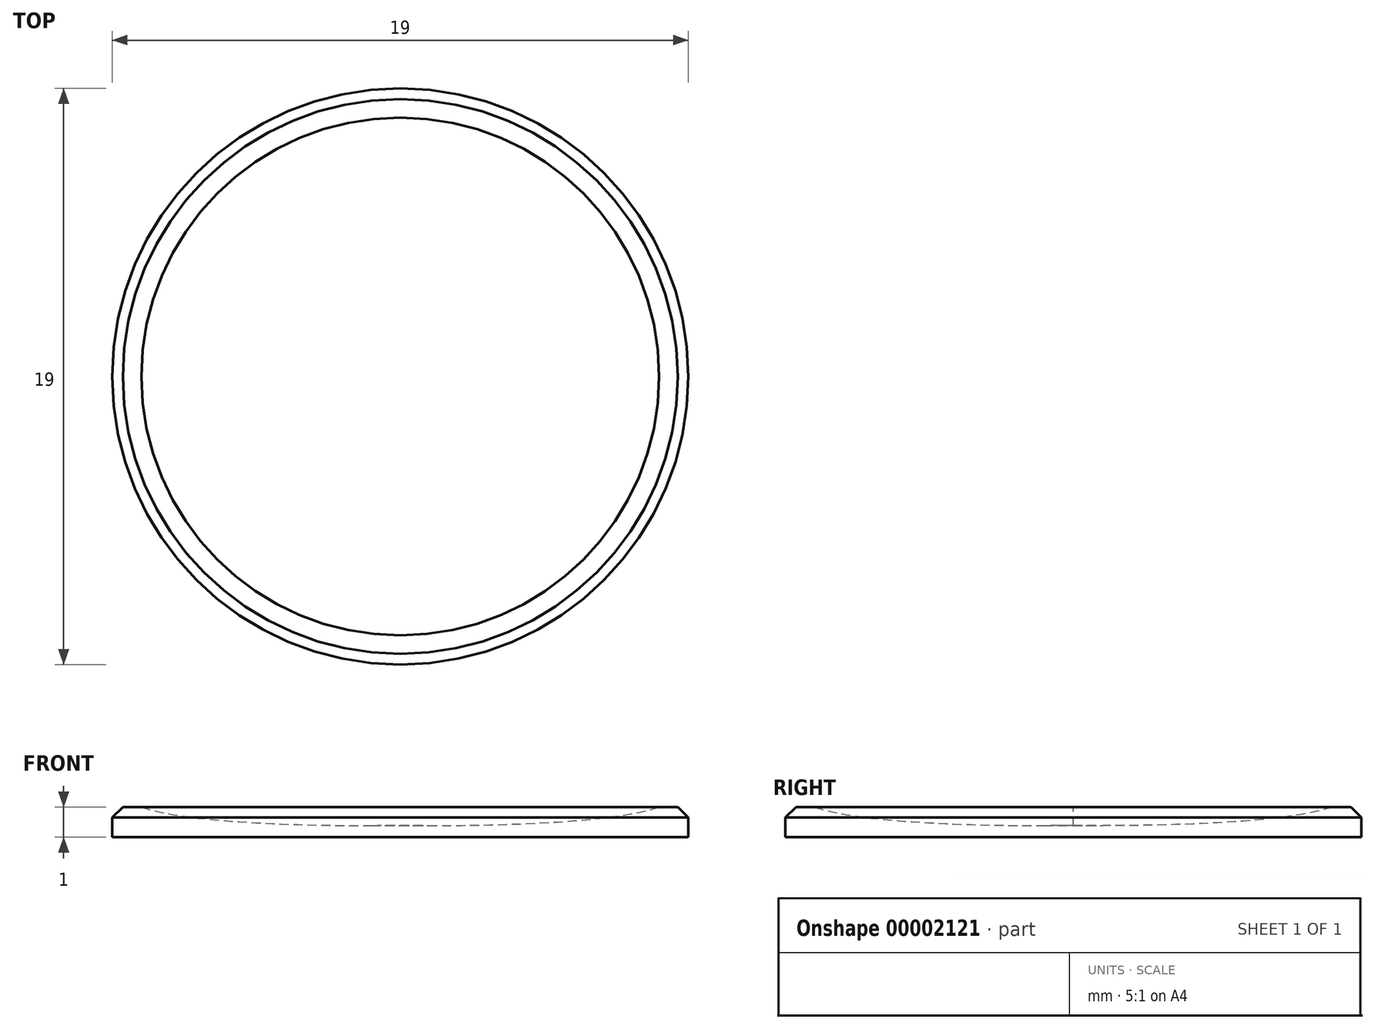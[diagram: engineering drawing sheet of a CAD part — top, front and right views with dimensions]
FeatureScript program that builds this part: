
annotation { "Feature Type Name" : "Feature", "Feature Type Description" : "" }
export const myFeature = defineFeature(function(context is Context, id is Id, definition is map)
    precondition{}
    {
        {
            var Q0;
            Q0=qCreatedBy(makeId("Top.planeOp"),FACE);
            var sketch = newSketch(context, id + "F0", { "sketchPlane" : qUnion([Q0])});
            skCircle(sketch, "E0", {"center": v(0, 0) * mm, "radius": 9.5 * mm});
            skSolve(sketch);
        }
        {
            var Q0;
            Q0=makeQuery(id+"F0.imprint","IMPRINT",FACE,{"disambiguationData":[TD([[makeQuery(id+"F0.imprint","IMPRINT",EDGE,{"derivedFrom":sQuery(id+"F0.wireOp",EDGE,"E0")}),1.0]])]});
            extrude(context, id + "F1", {"entities" : qUnion([Q0]), "depth" : 1 * mm});
        }
        {
            var Q0;
            Q0=qCreatedBy(makeId("Front.planeOp"),FACE);
            var sketch = newSketch(context, id + "F2", { "sketchPlane" : qUnion([Q0])});
            skLineSegment(sketch, "E1", {"start": v(0, 1.27) * mm, "end": v(0, 0.38) * mm});
            skLineSegment(sketch, "E2", {"start": v(9, 1.27) * mm, "end": v(0, 1.27) * mm});
            skLineSegment(sketch, "E3", {"start": v(0, 1.7) * mm, "end": v(0, 3.3) * mm, "construction": true});
            skFitSpline(sketch, "E4", {"points": [v(0, 0.38) * mm, v(0.9, 0.38) * mm, v(9, 1.27) * mm], "startDerivative": vector(10.77, 0) * mm, "endDerivative": vector(3.14, 3.55) * mm});
            skSolve(sketch);
        }
        {
            var Q0;
            Q0=qSketchRegion(id+"F2",true);
            var Q1;
            Q1=sQuery(id+"F2.wireOp",EDGE,"E3");
            revolve(context, id + "F3", {"operationType" : NewBodyOperationType.REMOVE, "entities" : qUnion([Q0]), "axis" : qUnion([Q1]), "revolveType" : RevolveType.FULL, "oppositeDirection" : true});
        }
        {
            var Q0;
            Q0=makeQuery(id+"F1.opExtrude","CAP_EDGE",EDGE,{"disambiguationData":[OSD([sQuery(id+"F0.wireOp",EDGE,"E0")])],"isStart":false});
            chamfer(context, id + "F4", {"entities" : qUnion([Q0]), "width" : .35 * mm, "tangentPropagation" : true});
        }
    });
